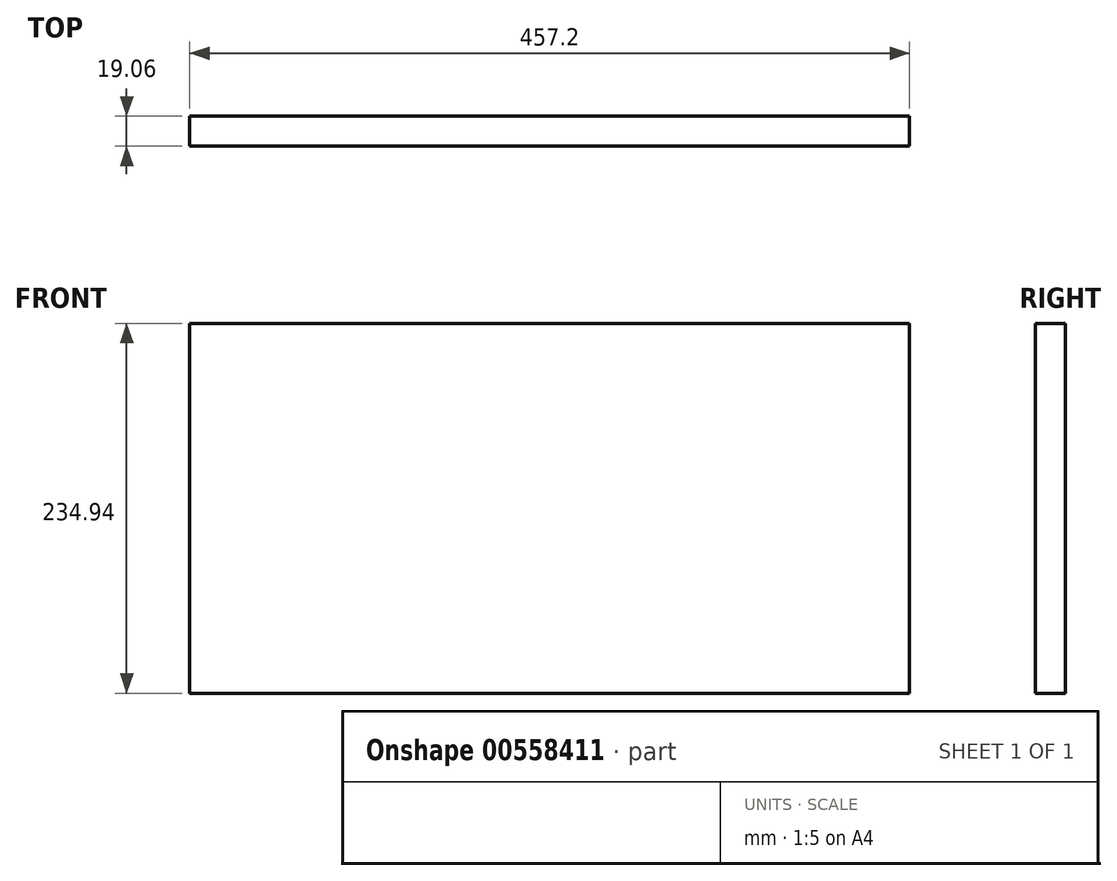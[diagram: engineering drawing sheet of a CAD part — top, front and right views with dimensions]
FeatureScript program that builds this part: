
annotation { "Feature Type Name" : "Feature", "Feature Type Description" : "" }
export const myFeature = defineFeature(function(context is Context, id is Id, definition is map)
    precondition{}
    {
        {
            var Q0;
            Q0=qCreatedBy(makeId("Front.planeOp"),FACE);
            var sketch = newSketch(context, id + "F0", { "sketchPlane" : qUnion([Q0])});
            skLineSegment(sketch, "E0.bottom", {"start": v(228.6, 117.48) * mm, "end": v(-228.6, 117.48) * mm});
            skLineSegment(sketch, "E0.top", {"start": v(228.6, -117.48) * mm, "end": v(-228.6, -117.48) * mm});
            skLineSegment(sketch, "E0.left", {"start": v(228.6, 117.48) * mm, "end": v(228.6, -117.48) * mm});
            skLineSegment(sketch, "E0.right", {"start": v(-228.6, 117.48) * mm, "end": v(-228.6, -117.48) * mm});
            skPoint(sketch, "E0.middle", {"position": v(0, 0) * mm});
            skSolve(sketch);
        }
        {
            var Q0;
            Q0=makeQuery(id+"F0.imprint","IMPRINT",FACE,{"disambiguationData":[TD([[makeQuery(id+"F0.imprint","IMPRINT",EDGE,{"derivedFrom":sQuery(id+"F0.wireOp",EDGE,"E0.bottom")}),1.0]])]});
            extrude(context, id + "F1", {"entities" : qUnion([Q0]), "endBound" : BoundingType.SYMMETRIC, "depth" : 19.05 * mm, "offsetDistance" : 25.4 * mm});
        }
    });
